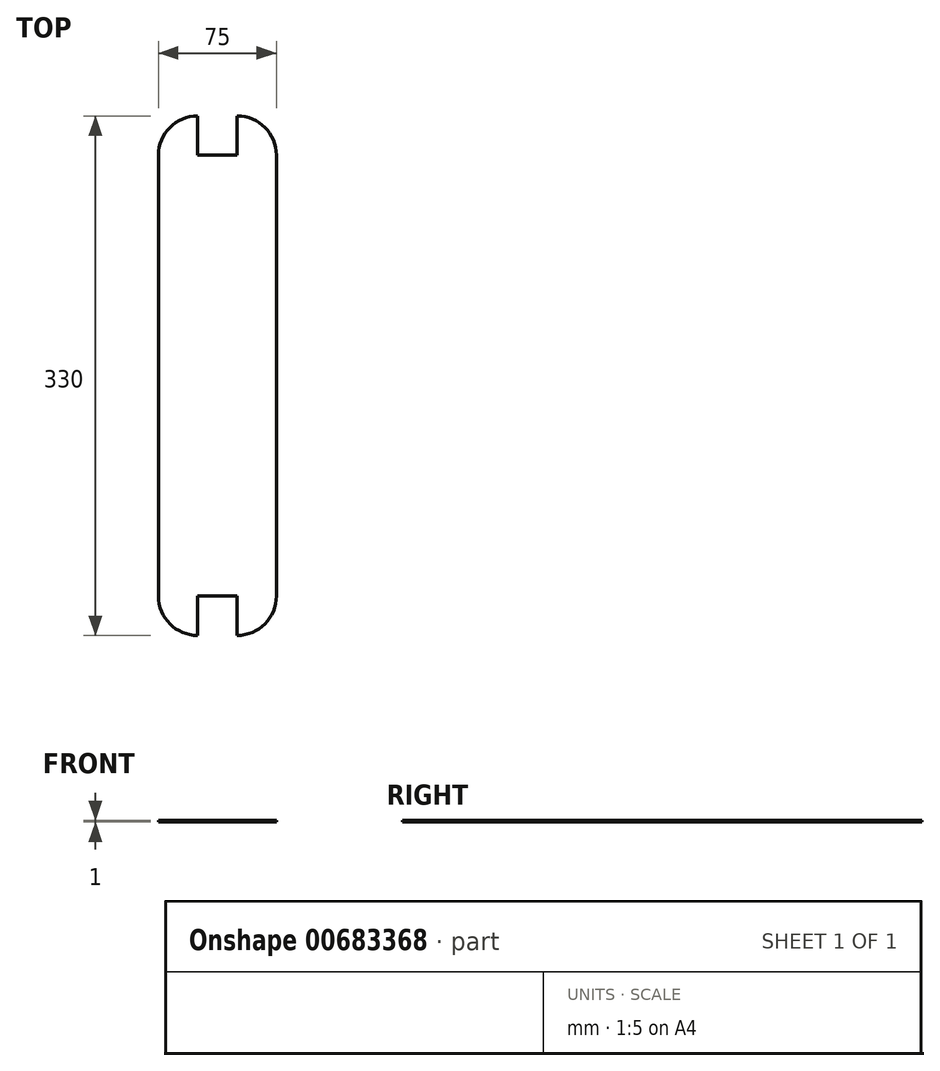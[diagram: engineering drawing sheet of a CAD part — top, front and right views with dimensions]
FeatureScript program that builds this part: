
annotation { "Feature Type Name" : "Feature", "Feature Type Description" : "" }
export const myFeature = defineFeature(function(context is Context, id is Id, definition is map)
    precondition{}
    {
        {
            var Q0;
            Q0=qCreatedBy(makeId("Top.planeOp"),FACE);
            var sketch = newSketch(context, id + "F0", { "sketchPlane" : qUnion([Q0])});
            skLineSegment(sketch, "E0.bottom", {"start": v(25.1, 305.05) * mm, "end": v(50.1, 305.05) * mm});
            skLineSegment(sketch, "E0.top", {"start": v(25.1, 25.05) * mm, "end": v(50.1, 25.05) * mm});
            skLineSegment(sketch, "E0.left", {"start": v(25.1, 305.05) * mm, "end": v(25.1, 25.05) * mm});
            skLineSegment(sketch, "E0.right", {"start": v(50.1, 305.05) * mm, "end": v(50.1, 25.05) * mm});
            skLineSegment(sketch, "E1.bottom", {"start": v(25.1, 305.05) * mm, "end": v(0.1, 305.05) * mm});
            skLineSegment(sketch, "E1.top", {"start": v(25.1, 25.05) * mm, "end": v(0.1, 25.05) * mm});
            skLineSegment(sketch, "E1.right", {"start": v(0.1, 305.05) * mm, "end": v(0.1, 25.05) * mm});
            skLineSegment(sketch, "E2.bottom", {"start": v(50.1, 305.05) * mm, "end": v(75.1, 305.05) * mm});
            skLineSegment(sketch, "E2.top", {"start": v(50.1, 25.05) * mm, "end": v(75.1, 25.05) * mm});
            skLineSegment(sketch, "E2.right", {"start": v(75.1, 305.05) * mm, "end": v(75.1, 25.05) * mm});
            skLineSegment(sketch, "E3.top", {"start": v(25.1, 330.05) * mm, "end": v(50.1, 330.05) * mm});
            skLineSegment(sketch, "E3.left", {"start": v(25.1, 305.05) * mm, "end": v(25.1, 330.05) * mm});
            skLineSegment(sketch, "E3.right", {"start": v(50.1, 305.05) * mm, "end": v(50.1, 330.05) * mm});
            skLineSegment(sketch, "E4.top", {"start": v(25.1, 0.05) * mm, "end": v(50.1, 0.05) * mm});
            skLineSegment(sketch, "E4.left", {"start": v(25.1, 25.05) * mm, "end": v(25.1, 0.05) * mm});
            skLineSegment(sketch, "E4.right", {"start": v(50.1, 25.05) * mm, "end": v(50.1, 0.05) * mm});
            skArc(sketch, "E5", {"start": v(25.1, 330.05) * mm, "mid": v(7.41, 322.73) * mm, "end": v(0.1, 305.05) * mm});
            skArc(sketch, "E6", {"start": v(50.1, 330.05) * mm, "mid": v(67.77, 322.73) * mm, "end": v(75.1, 305.05) * mm});
            skArc(sketch, "E7", {"start": v(75.1, 25.05) * mm, "mid": v(67.77, 7.37) * mm, "end": v(50.1, 0.05) * mm});
            skArc(sketch, "E8", {"start": v(25.1, 0.05) * mm, "mid": v(7.41, 7.37) * mm, "end": v(0.1, 25.05) * mm});
            skSolve(sketch);
        }
        {
            var Q0;
            Q0=makeQuery(id+"F0.imprint","IMPRINT",FACE,{"disambiguationData":[TD([[makeQuery(id+"F0.imprint","IMPRINT",EDGE,{"derivedFrom":sQuery(id+"F0.wireOp",EDGE,"E0.left")}),-1.0]])]});
            var Q1;
            Q1=makeQuery(id+"F0.imprint","IMPRINT",FACE,{"disambiguationData":[TD([[makeQuery(id+"F0.imprint","IMPRINT",EDGE,{"derivedFrom":sQuery(id+"F0.wireOp",EDGE,"E0.left")}),1.0]])]});
            var Q2;
            Q2=makeQuery(id+"F0.imprint","IMPRINT",FACE,{"disambiguationData":[TD([[makeQuery(id+"F0.imprint","IMPRINT",EDGE,{"derivedFrom":sQuery(id+"F0.wireOp",EDGE,"E2.bottom")}),-1.0]])]});
            var Q3;
            Q3=makeQuery(id+"F0.imprint","IMPRINT",FACE,{"disambiguationData":[TD([[makeQuery(id+"F0.imprint","IMPRINT",EDGE,{"derivedFrom":sQuery(id+"F0.wireOp",EDGE,"E2.top")}),-1.0]])]});
            var Q4;
            Q4=makeQuery(id+"F0.imprint","IMPRINT",FACE,{"disambiguationData":[TD([[makeQuery(id+"F0.imprint","IMPRINT",EDGE,{"derivedFrom":sQuery(id+"F0.wireOp",EDGE,"E0.top")}),-1.0]])]});
            var Q5;
            Q5=makeQuery(id+"F0.imprint","IMPRINT",FACE,{"disambiguationData":[TD([[makeQuery(id+"F0.imprint","IMPRINT",EDGE,{"derivedFrom":sQuery(id+"F0.wireOp",EDGE,"E1.top")}),1.0]])]});
            var Q6;
            Q6=makeQuery(id+"F0.imprint","IMPRINT",FACE,{"disambiguationData":[TD([[makeQuery(id+"F0.imprint","IMPRINT",EDGE,{"derivedFrom":sQuery(id+"F0.wireOp",EDGE,"E1.bottom")}),-1.0]])]});
            var Q7;
            Q7=makeQuery(id+"F0.imprint","IMPRINT",FACE,{"disambiguationData":[TD([[makeQuery(id+"F0.imprint","IMPRINT",EDGE,{"derivedFrom":sQuery(id+"F0.wireOp",EDGE,"E0.bottom")}),1.0]])]});
            var Q8;
            Q8=makeQuery(id+"F0.imprint","IMPRINT",FACE,{"disambiguationData":[TD([[makeQuery(id+"F0.imprint","IMPRINT",EDGE,{"derivedFrom":sQuery(id+"F0.wireOp",EDGE,"E2.bottom")}),1.0]])]});
            extrude(context, id + "F1", {"entities" : qUnion([Q0, Q1, Q2, Q3, Q4, Q5, Q6, Q7, Q8]), "depth" : 1 * mm, "offsetDistance" : 25 * mm});
        }
    });
